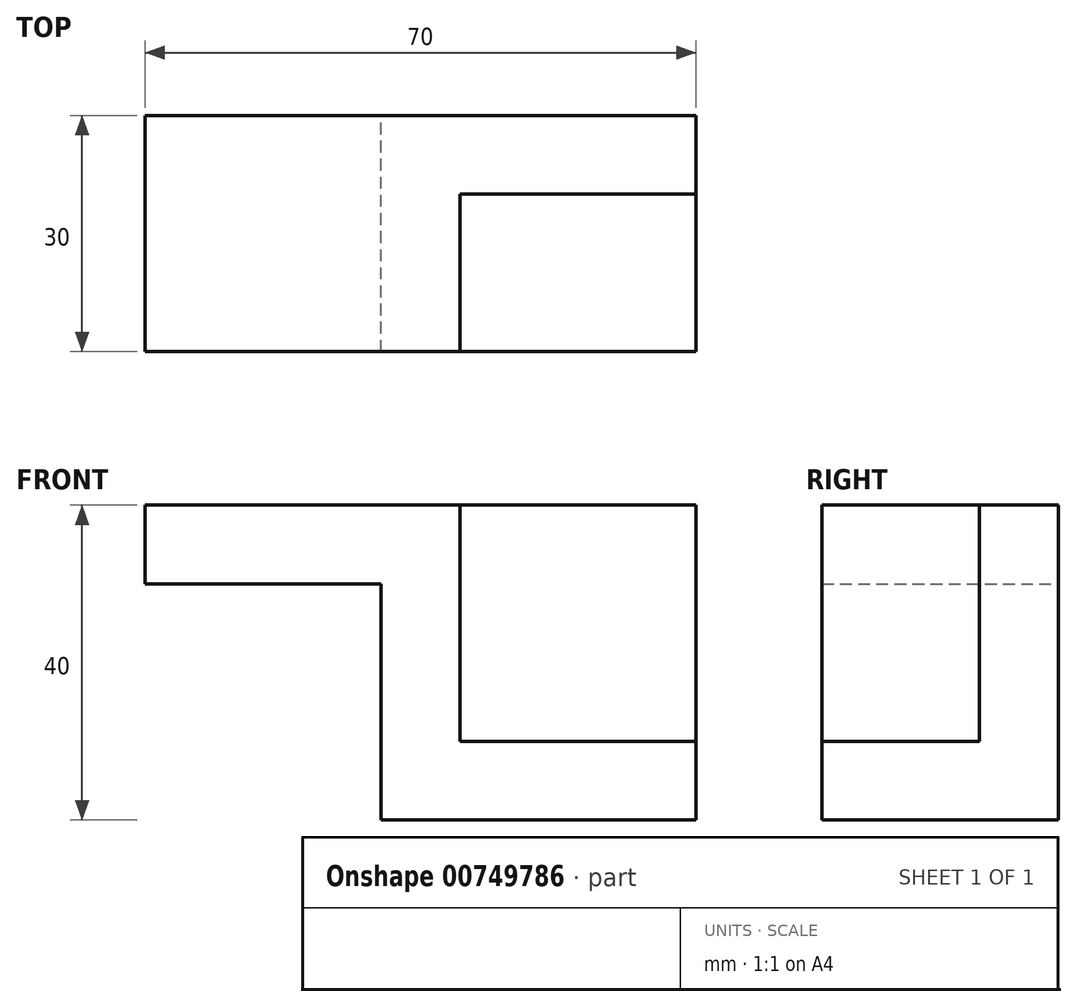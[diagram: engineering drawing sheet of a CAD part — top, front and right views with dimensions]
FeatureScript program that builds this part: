
annotation { "Feature Type Name" : "Feature", "Feature Type Description" : "" }
export const myFeature = defineFeature(function(context is Context, id is Id, definition is map)
    precondition{}
    {
        {
            var Q0;
            Q0=qCreatedBy(makeId("Front.planeOp"),FACE);
            var sketch = newSketch(context, id + "F0", { "sketchPlane" : qUnion([Q0])});
            skLineSegment(sketch, "E0", {"start": v(0, 0) * mm, "end": v(0, 10) * mm});
            skLineSegment(sketch, "E1", {"start": v(0, 10) * mm, "end": v(70, 10) * mm});
            skLineSegment(sketch, "E2", {"start": v(70, 10) * mm, "end": v(70, -30) * mm});
            skLineSegment(sketch, "E3", {"start": v(70, -30) * mm, "end": v(30, -30) * mm});
            skLineSegment(sketch, "E4", {"start": v(30, -30) * mm, "end": v(30, 0) * mm});
            skLineSegment(sketch, "E5", {"start": v(30, 0) * mm, "end": v(0, 0) * mm});
            skSolve(sketch);
        }
        {
            var Q0;
            Q0=makeQuery(id+"F0.imprint","IMPRINT",FACE,{"disambiguationData":[TD([[makeQuery(id+"F0.imprint","IMPRINT",EDGE,{"derivedFrom":sQuery(id+"F0.wireOp",EDGE,"E0")}),-1.0]])]});
            extrude(context, id + "F1", {"entities" : qUnion([Q0]), "depth" : 30 * mm, "offsetDistance" : 25 * mm});
        }
        {
            var Q0;
            Q0=makeQuery(id+"F1.opExtrude","CAP_FACE",FACE,{"disambiguationData":[OSD([sQuery(id+"F0.wireOp",EDGE,"E0"),sQuery(id+"F0.wireOp",EDGE,"E1"),sQuery(id+"F0.wireOp",EDGE,"E2"),sQuery(id+"F0.wireOp",EDGE,"E3"),sQuery(id+"F0.wireOp",EDGE,"E4"),sQuery(id+"F0.wireOp",EDGE,"E5")])],"isStart":false});
            var sketch = newSketch(context, id + "F2", { "sketchPlane" : qUnion([Q0])});
            skLineSegment(sketch, "E6", {"start": v(70, 10) * mm, "end": v(70, -20) * mm});
            skLineSegment(sketch, "E7", {"start": v(70, -20) * mm, "end": v(40, -20) * mm});
            skLineSegment(sketch, "E8", {"start": v(40, -20) * mm, "end": v(40, 10) * mm});
            skSolve(sketch);
        }
        {
            var Q0;
            {var subQ0=sQuery(id+"F2.wireOp",EDGE,"E6");Q0=makeQuery(id+"F2.imprint","IMPRINT",FACE,{"disambiguationData":[TD([[makeQuery(id+"F2.imprint","IMPRINT",EDGE,{"derivedFrom":subQ0}),-1.0]])]});}
            extrude(context, id + "F3", {"entities" : qUnion([Q0]), "operationType" : NewBodyOperationType.REMOVE, "oppositeDirection" : true, "depth" : 20 * mm, "offsetDistance" : 25 * mm});
        }
    });
